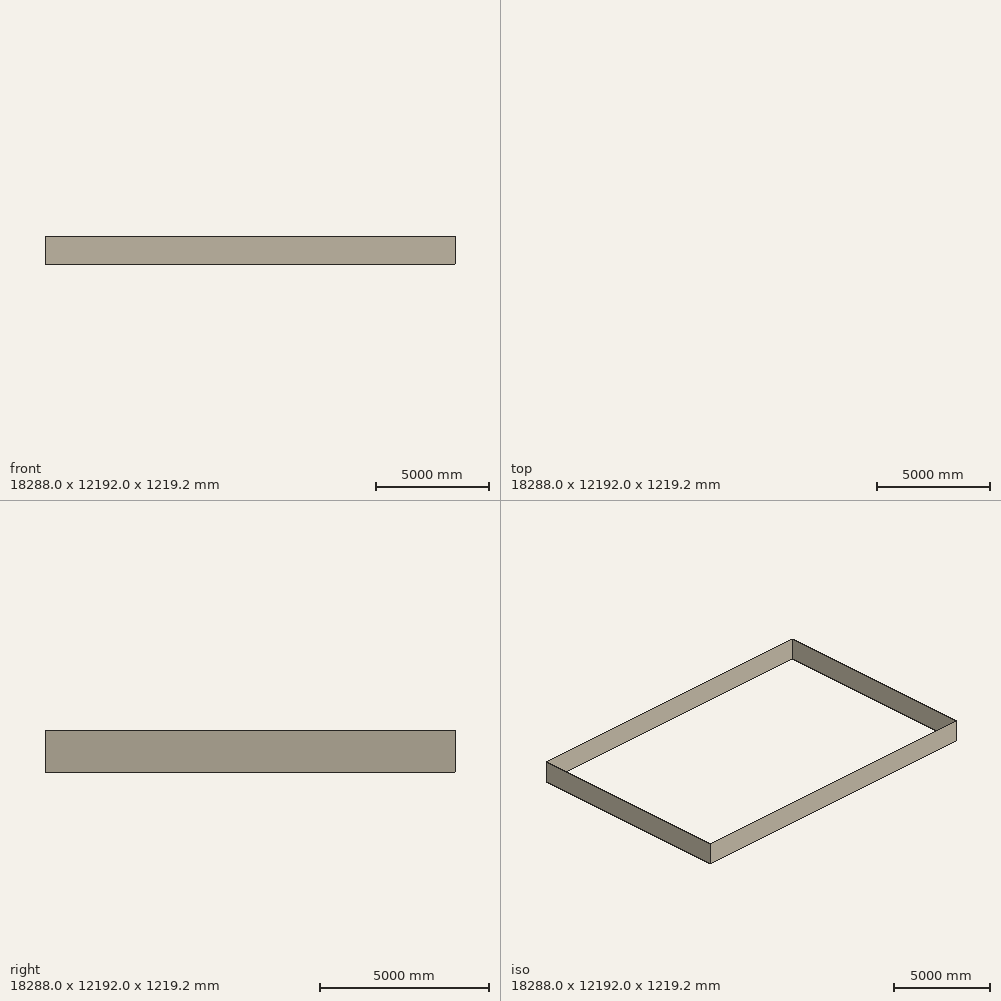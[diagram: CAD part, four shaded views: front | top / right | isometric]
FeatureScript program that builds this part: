
annotation { "Feature Type Name" : "Feature", "Feature Type Description" : "" }
export const myFeature = defineFeature(function(context is Context, id is Id, definition is map)
    precondition{}
    {
        {
            var Q0;
            Q0=qCreatedBy(makeId("Top.planeOp"),FACE);
            var sketch = newSketch(context, id + "F0", { "sketchPlane" : qUnion([Q0])});
            skLineSegment(sketch, "E0.bottom", {"start": v(9144, -6096) * mm, "end": v(-9144, -6096) * mm});
            skLineSegment(sketch, "E0.top", {"start": v(9144, 6096) * mm, "end": v(-9144, 6096) * mm});
            skLineSegment(sketch, "E0.left", {"start": v(9144, -6096) * mm, "end": v(9144, 6096) * mm});
            skLineSegment(sketch, "E0.right", {"start": v(-9144, -6096) * mm, "end": v(-9144, 6096) * mm});
            skPoint(sketch, "E0.middle", {"position": v(0, 0) * mm});
            skSolve(sketch);
        }
        {
            var Q0;
            Q0 = qSketchRegion(id + "F0", true);
            extrude(context, id + "F1", {"entities" : qUnion([Q0]), "depth" : 1219.2 * mm, "offsetDistance" : 25.4 * mm});
        }
        {
            var Q0;
            Q0=makeQuery(id+"F1.opExtrude","CAP_FACE",FACE,{"disambiguationData":[OSD([sQuery(id+"F0.wireOp",EDGE,"E0.bottom"),sQuery(id+"F0.wireOp",EDGE,"E0.top"),sQuery(id+"F0.wireOp",EDGE,"E0.left"),sQuery(id+"F0.wireOp",EDGE,"E0.right")])],"isStart":false});
            var Q1;
            Q1=makeQuery(id+"F1.opExtrude","CAP_FACE",FACE,{"disambiguationData":[OSD([sQuery(id+"F0.wireOp",EDGE,"E0.bottom"),sQuery(id+"F0.wireOp",EDGE,"E0.top"),sQuery(id+"F0.wireOp",EDGE,"E0.left"),sQuery(id+"F0.wireOp",EDGE,"E0.right")])],"isStart":true});
            shell(context, id + "F2", {"entities" : qUnion([Q0, Q1]), "thickness" : 2.54 * mm});
        }
    });
